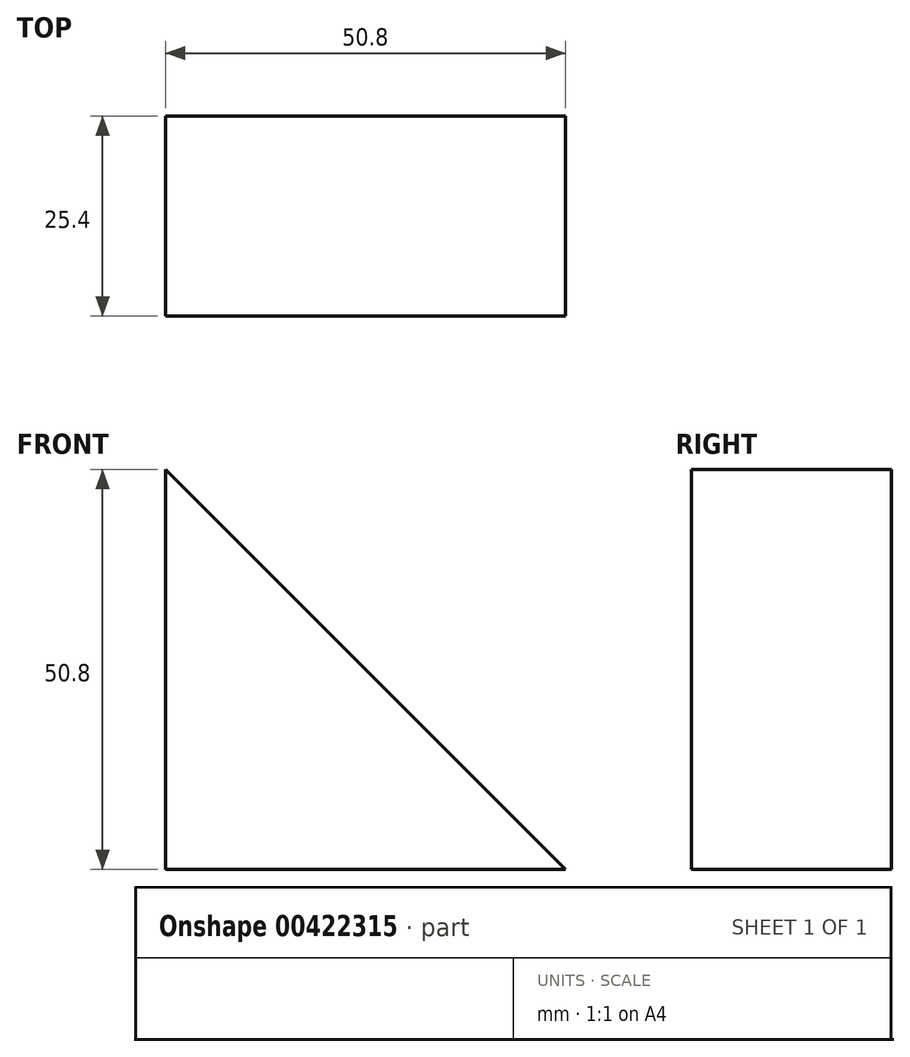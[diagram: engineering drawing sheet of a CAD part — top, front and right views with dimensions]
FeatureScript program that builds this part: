
annotation { "Feature Type Name" : "Feature", "Feature Type Description" : "" }
export const myFeature = defineFeature(function(context is Context, id is Id, definition is map)
    precondition{}
    {
        {
            var Q0;
            Q0=qCreatedBy(makeId("Front.planeOp"),FACE);
            var sketch = newSketch(context, id + "F0", { "sketchPlane" : qUnion([Q0])});
            skLineSegment(sketch, "E0", {"start": v(0, 0) * mm, "end": v(0, 50.8) * mm});
            skLineSegment(sketch, "E1", {"start": v(0, 0) * mm, "end": v(50.8, 0) * mm});
            skLineSegment(sketch, "E2", {"start": v(0, 50.8) * mm, "end": v(50.8, 0) * mm});
            skSolve(sketch);
        }
        {
            var Q0;
            Q0 = qSketchRegion(id + "F0", true);
            extrude(context, id + "F1", {"entities" : qUnion([Q0]), "depth" : 25.4 * mm});
        }
    });
